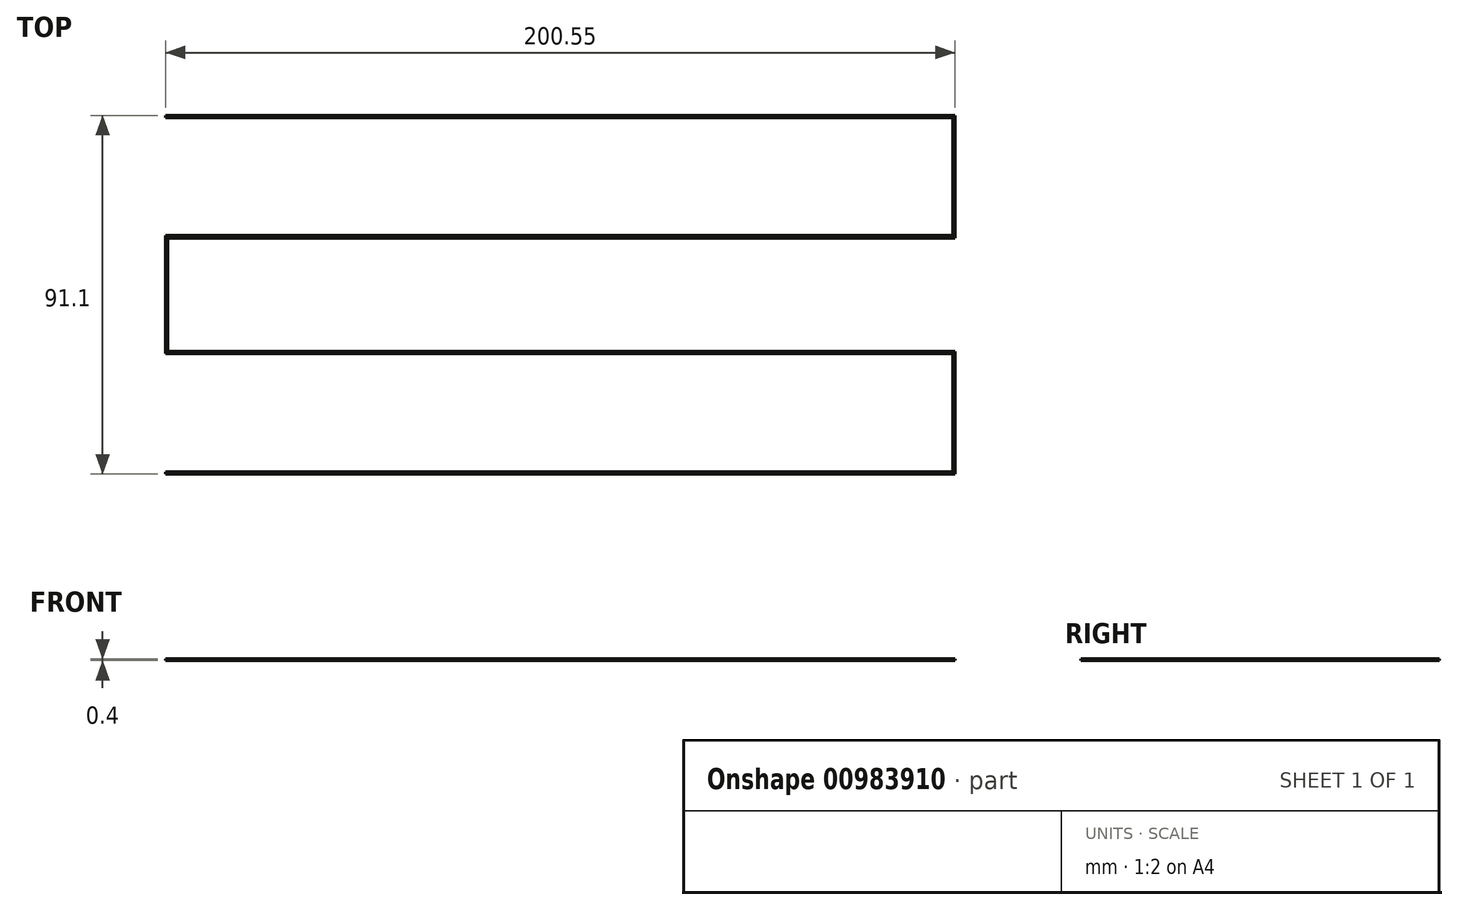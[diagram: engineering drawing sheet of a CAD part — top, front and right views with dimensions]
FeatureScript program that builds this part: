
annotation { "Feature Type Name" : "Feature", "Feature Type Description" : "" }
export const myFeature = defineFeature(function(context is Context, id is Id, definition is map)
    precondition{}
    {
        {
            var Q0;
            Q0=qCreatedBy(makeId("Top.planeOp"),FACE);
            var sketch = newSketch(context, id + "F0", { "sketchPlane" : qUnion([Q0])});
            skLineSegment(sketch, "E0", {"start": v(0, 0) * mm, "end": v(200, 0) * mm});
            skLineSegment(sketch, "E1", {"start": v(200, 0) * mm, "end": v(200, 30) * mm});
            skLineSegment(sketch, "E2", {"start": v(200, 30) * mm, "end": v(0, 30) * mm});
            skLineSegment(sketch, "E3", {"start": v(0, 30) * mm, "end": v(0, 60) * mm});
            skLineSegment(sketch, "E4", {"start": v(0, 60) * mm, "end": v(200, 60) * mm});
            skLineSegment(sketch, "E5", {"start": v(200, 60) * mm, "end": v(200, 90) * mm});
            skLineSegment(sketch, "E6", {"start": v(200, 90) * mm, "end": v(0, 90) * mm});
            skLineSegment(sketch, "E7.0", {"start": v(200.55, 90.55) * mm, "end": v(0, 90.55) * mm});
            skLineSegment(sketch, "E7.1", {"start": v(200.55, 59.45) * mm, "end": v(200.55, 90.55) * mm});
            skLineSegment(sketch, "E7.2", {"start": v(0.55, 59.45) * mm, "end": v(200.55, 59.45) * mm});
            skLineSegment(sketch, "E7.3", {"start": v(0, -0.55) * mm, "end": v(200.55, -0.55) * mm});
            skLineSegment(sketch, "E7.4", {"start": v(200.55, -0.55) * mm, "end": v(200.55, 30.55) * mm});
            skLineSegment(sketch, "E7.5", {"start": v(200.55, 30.55) * mm, "end": v(0.55, 30.55) * mm});
            skLineSegment(sketch, "E7.6", {"start": v(0.55, 30.55) * mm, "end": v(0.55, 59.45) * mm});
            skLineSegment(sketch, "E8", {"start": v(0, 90) * mm, "end": v(0, 90.55) * mm});
            skLineSegment(sketch, "E9", {"start": v(0, -0.55) * mm, "end": v(0, 0) * mm});
            skSolve(sketch);
        }
        {
            var Q0;
            Q0 = qSketchRegion(id + "F0", true);
            extrude(context, id + "F1", {"entities" : qUnion([Q0]), "depth" : .40 * mm, "offsetDistance" : 25 * mm});
        }
    });
